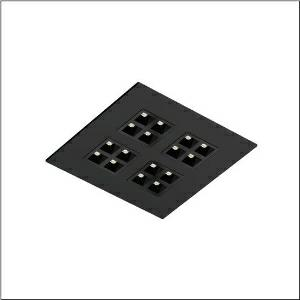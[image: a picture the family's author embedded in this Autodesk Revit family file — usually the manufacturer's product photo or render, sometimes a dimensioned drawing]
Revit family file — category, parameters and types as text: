
# Revit family: silica_31_square_51my6lms44ba
name_source: partatom
category: Lighting Fixtures
units: mm (PartAtom-declared; Revit-internal decimal feet)

## family parameters
Cut with Voids When Loaded = No
Host = Face
Light Source = No
Part Type = Normal
Room Calculation Point = No
Round Connector Dimension = Use Diameter
Shared = No

## types (1)
- --- (1 x LED, 6620 lm, 39 W, 4000K)
    Apparent Load = 39 VA
    CIE Flux Codes = 82 100 100 100 100
    Color Rendering = 80
    Color Temperature = 4000K
    Default Elevation = 1800 mm
    Description = Silica 31 Square, office luminaire, primary light control with lens, of PMMA, primary anti-glare with reflector, of PC, black, light emission: direct distribution, primary light characteristic: symmetric, installation type: lay-in mounting, LED, rated luminous flux: 4.610lm, luminous efficacy: 177lm/W, light colour: 840, colour temperature: 4000K, control gear: ON/OFF Multilumen, with terminal, 3-pole, mains connection: 220..240V, AC, 50/60Hz, rated input power: 26W, luminaire housing, of sheet steel, coated, jet black (RAL 9005), module: M600, length: 595mm, width: 595mm, height: 43mm, protection rating (complete): IP20, insulation class (complete): insulation class II (safety insulation), certification: CE, impact resistance: IK03, permissible operating ambient temperature: -20..+35°C, standard: EN 50419, packaging unit: 1 piece
    Height = 0 mm  [stored 0 ft]
    Lamp = 1 x LED
    Lamp Light Flux = 6620 lm
    Lamp Power = 39 W
    Lamp count = 1
    Length = 595 mm
    Luminous efficacy = 170 lm/W
    Manufacturer = Siteco
    ModVariant = No
    Model = 51MY6LMS44BA
    Mounting Place = Ceiling
    Mounting Type = Recessed
    Number of Poles = 1
    OnlyDefault = Yes
    Power Factor = 1
    Product Name = Silica 31 Square
    Product group = office luminaire | ceiling recessed
    ProductGroupID = 400
    Protection Class = Protection class II
    Protection Degree = IP 20
    RLX_Detail_Level = 1
    RLX_Emergency_Light_Flux = 0 lm
    RLX_Emergency_Type = 0
    RLX_Emergency_Type_DB = No
    RlxData = <blob elided: 36069 chars, md5=e48457e7>
    Socket = socket
    Standby Power = 0 W
    System Light Flux = 6620 lm
    System Power = 39 W
    Type Comments = factory setting: luminous flux: 100 % | (ON | ON | ON | ON) | 1100 mA
    Type Image = l_1313660.jpg
    URL = http://relux.com
    VarID = @adj_043249
    Voltage = 0 V
    Weight = 0.00 kg
    Width = 595 mm

note: [stored X ft] marks values corroborated as IEEE doubles in the binary element streams (Revit-internal decimal feet)

## geometry (parser evidence)
native form markers: Blend x4, Sweep x9
no freeform markers — native parametric forms only
